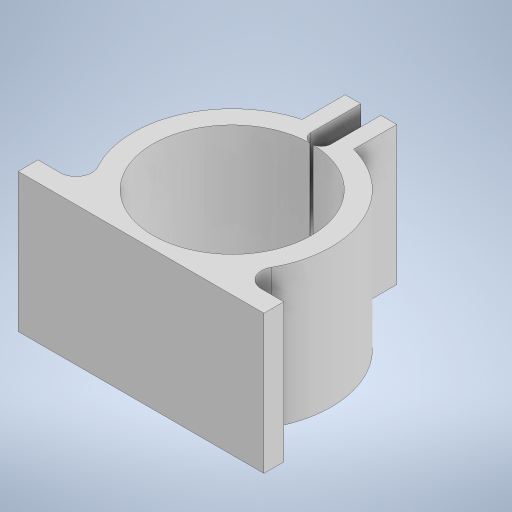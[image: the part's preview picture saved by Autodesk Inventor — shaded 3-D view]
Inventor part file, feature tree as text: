
AUTODESK INVENTOR PART (.ipt)
format: ipt  version: 2024 (Build 280153000, 153)  size: 355,328 bytes
history: native  units: mm
features: sketch x12, extrude x11, projected_geometry x4, fillet x1
ambient origin geometry x8: Origin, YZ Plane, XZ Plane, XY Plane, X Axis, Y Axis, Z Axis, Center Point
bodies: Solid1 (feature_tree)
feature tree (28):
  extrude  "Extrusion1"  Depth=70.0mm TaperAngle=0.0deg
  extrude  "Extrusion2"  TaperAngle=0.0deg  [1 undecoded]
  extrude  "Extrusion3"  Depth=6.0mm
  extrude  "Extrusion4"  Depth=70.0mm TaperAngle=0.0deg
  extrude  "Extrusion6"  Depth=70.0mm TaperAngle=0.0deg
  extrude  "Extrusion7"  Depth=70.0mm TaperAngle=0.0deg
  extrude  "Extrusion8"  Depth=70.0mm TaperAngle=0.0deg
  extrude  "Extrusion9"  [1 undecoded]
  sketch  "Sketch10"
  fillet  "Fillet1"  [1 undecoded]
  extrude  "Extrusion10"  [1 undecoded]
  extrude  "Extrusion11"  [1 undecoded]
  extrude  "Extrusion12"  [1 undecoded]
  sketch  "Sketch1"  dims[d0=100.0mm d1=70.0mm d2=0.0mm]
  sketch  "Sketch2"  dims[d3=100.0mm d4=0.0mm d5=0.0mm d6=0.0mm]
  sketch  "Sketch3"  dims[d7=6.0mm d8=0.0mm d9=6.1mm]
  sketch  "Sketch4"  dims[d12=70.0mm d13=0.0mm d14=70.0mm d15=0.0mm]
  sketch  "Sketch6"  dims[d16=10.0mm d17=0.0mm d18=70.0mm d19=0.0mm]
  sketch  "Sketch7"  dims[d20=8.0mm d21=70.0mm d22=0.0mm]
  sketch  "Sketch8"  dims[d23=70.0mm d24=0.0mm d25=70.0mm d26=0.0mm]
  projected_geometry  "Projected Loop2"
  projected_geometry  "Projected Loop3"
  sketch  "Sketch9"
  sketch  "Sketch11"
  sketch  "Sketch12"
  projected_geometry  "Projected Loop4"
  projected_geometry  "Projected Loop5"
  sketch  "Sketch13"
note: 6 required parameter values undecoded (feature->parameter linkage not recoverable at this tier; creation-order binding heuristic only, values carry confidence <= 0.55)
